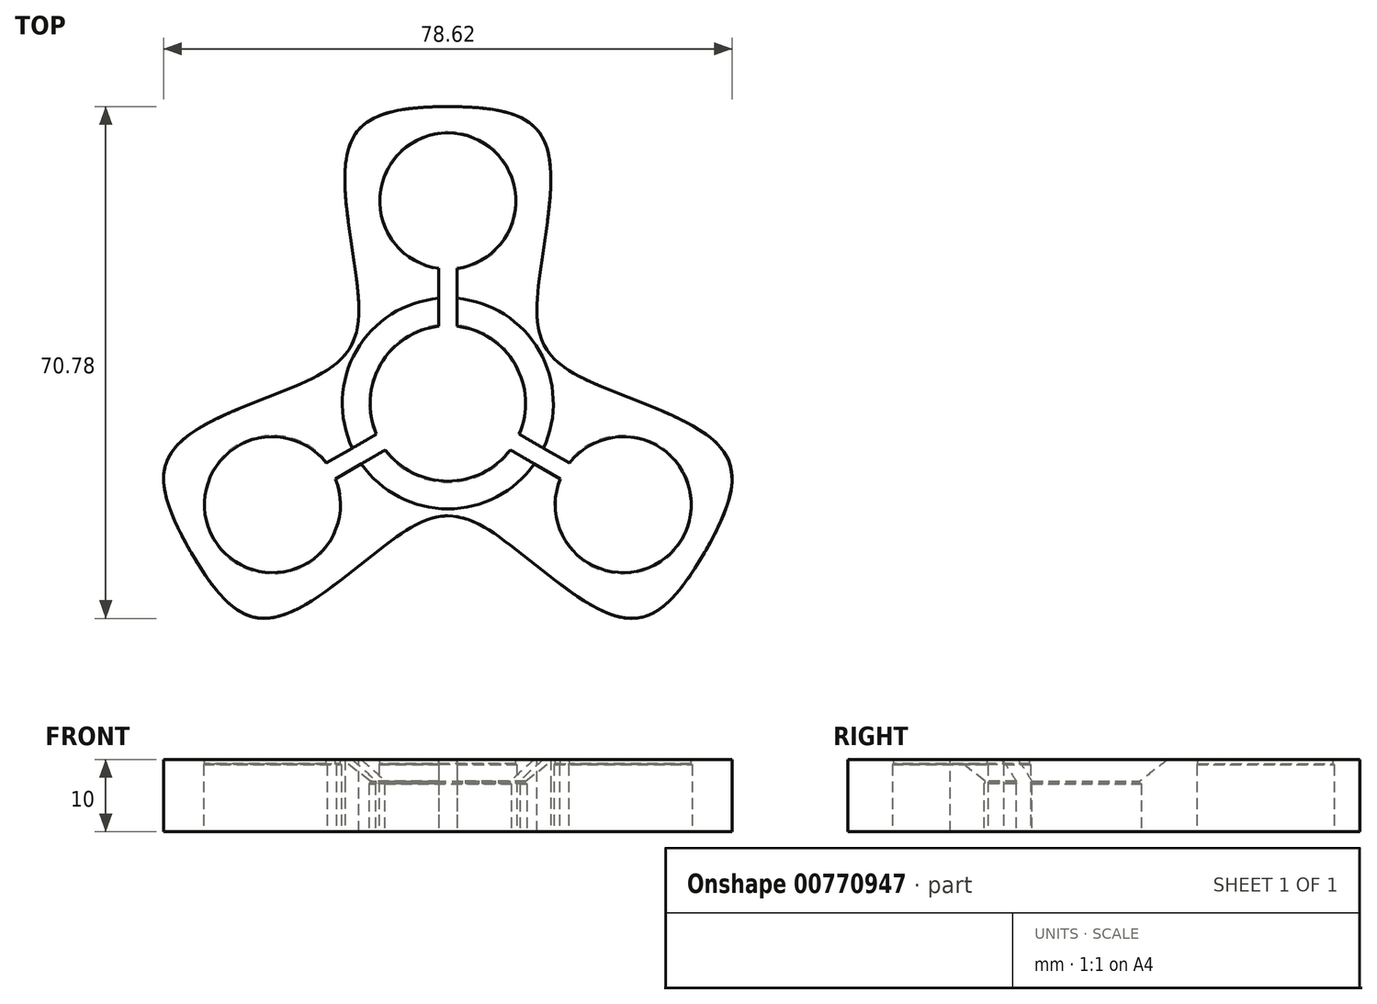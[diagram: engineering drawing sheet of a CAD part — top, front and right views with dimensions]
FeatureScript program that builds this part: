
annotation { "Feature Type Name" : "Feature", "Feature Type Description" : "" }
export const myFeature = defineFeature(function(context is Context, id is Id, definition is map)
    precondition{}
    {
        {
            assignVariable(context, id + "F0", {"name" : "ledge", "anyValue" : 0.15});
        }
        {
            var Q0;
            Q0=qCreatedBy(makeId("Top.planeOp"),FACE);
            var sketch = newSketch(context, id + "F1", { "sketchPlane" : qUnion([Q0])});
            skLineSegment(sketch, "E0", {"start": v(0, 0) * mm, "end": v(71.1, 41.05) * mm, "construction": true});
            skLineSegment(sketch, "E1", {"start": v(0, 0) * mm, "end": v(-71.1, 41.05) * mm, "construction": true});
            skCircle(sketch, "E2", {"center": v(0, 0) * mm, "radius": 10.9 * mm, "construction": true});
            skCircle(sketch, "E3", {"center": v(0, 28) * mm, "radius": 9.55 * mm});
            skLineSegment(sketch, "E4", {"start": v(-16, 41.05) * mm, "end": v(16, 41.05) * mm});
            skLineSegment(sketch, "E5", {"start": v(16, 41.05) * mm, "end": v(11.13, 6.43) * mm});
            skLineSegment(sketch, "E6", {"start": v(-16, 41.05) * mm, "end": v(-11.13, 6.43) * mm});
            skLineSegment(sketch, "E7", {"start": v(0, 28) * mm, "end": v(0, 41.05) * mm, "construction": true});
            skPoint(sketch, "E8", {"position": v(0, 37.55) * mm});
            skArc(sketch, "E9", {"start": v(9.44, 5.45) * mm, "mid": v(0, 10.9) * mm, "end": v(-9.44, 5.45) * mm});
            skLineSegment(sketch, "E10", {"start": v(-9.44, 5.45) * mm, "end": v(-11.13, 6.43) * mm});
            skLineSegment(sketch, "E11", {"start": v(9.44, 5.45) * mm, "end": v(11.13, 6.43) * mm});
            skSolve(sketch);
        }
        {
            var Q0;
            Q0=qSketchRegion(id+"F1",true);
            extrude(context, id + "F2", {"entities" : qUnion([Q0]), "endBound" : BoundingType.SYMMETRIC, "depth" : 7 * mm, "offsetDistance" : 25 * mm});
        }
        {
            var Q0;
            Q0=makeQuery(id+"F2.opExtrude","SWEPT_EDGE",EDGE,{"disambiguationData":[OSD([sQuery(id+"F1.wireOp",EDGE,"E4"),sQuery(id+"F1.wireOp",EDGE,"E6")])]});
            var Q1;
            Q1=makeQuery(id+"F2.opExtrude","SWEPT_EDGE",EDGE,{"disambiguationData":[OSD([sQuery(id+"F1.wireOp",EDGE,"E4"),sQuery(id+"F1.wireOp",EDGE,"E5")])]});
            fillet(context, id + "F3", {"entities" : qUnion([Q0, Q1]), "radius" : 14 * mm, "tangentPropagation" : true, "rho" : .6, "crossSection" : FilletCrossSection.CONIC, "allowEdgeOverflow" : false});
        }
        {
            var Q0;
            Q0=makeQuery(id+"F2.opExtrude","CAP_FACE",FACE,{"disambiguationData":[OSD([sQuery(id+"F1.wireOp",EDGE,"E3"),sQuery(id+"F1.wireOp",EDGE,"E4"),sQuery(id+"F1.wireOp",EDGE,"E5"),sQuery(id+"F1.wireOp",EDGE,"E6"),sQuery(id+"F1.wireOp",EDGE,"E9"),sQuery(id+"F1.wireOp",EDGE,"E10"),sQuery(id+"F1.wireOp",EDGE,"E11")])],"isStart":false});
            var sketch = newSketch(context, id + "F4", { "sketchPlane" : qUnion([Q0])});
            skCircle(sketch, "E12.0", {"center": v(0, 28) * mm, "radius": 9.55 * mm});
            skCircle(sketch, "E13.0", {"center": v(0, 28) * mm, "radius": 9.4 * mm});
            skArc(sketch, "E14.0", {"start": v(9.44, 5.45) * mm, "mid": v(0, 10.9) * mm, "end": v(-9.44, 5.45) * mm});
            skArc(sketch, "E15.0", {"start": v(9.3, 5.37) * mm, "mid": v(0, 10.75) * mm, "end": v(-9.3, 5.37) * mm});
            skLineSegment(sketch, "E16", {"start": v(-9.3, 5.37) * mm, "end": v(-9.44, 5.45) * mm});
            skLineSegment(sketch, "E17", {"start": v(9.3, 5.37) * mm, "end": v(9.44, 5.45) * mm});
            skSolve(sketch);
        }
        {
            var Q0;
            Q0=makeQuery(id+"F4.imprint","IMPRINT",FACE,{"disambiguationData":[TD([[makeQuery(id+"F4.imprint","IMPRINT",EDGE,{"derivedFrom":sQuery(id+"F4.wireOp",EDGE,"E14.0")}),1.0]])]});
            extrude(context, id + "F5", {"entities" : qUnion([Q0]), "operationType" : NewBodyOperationType.ADD, "oppositeDirection" : true, "depth" : .4 * mm, "offsetDistance" : 25 * mm});
        }
        {
            var Q0;
            Q0=makeQuery(id+"F5.boolean.opBoolean","MERGE",FACE,{"derivedFrom":[makeQuery(id+"F2.opExtrude","CAP_FACE",FACE,{"disambiguationData":[OSD([sQuery(id+"F1.wireOp",EDGE,"E3"),sQuery(id+"F1.wireOp",EDGE,"E4"),sQuery(id+"F1.wireOp",EDGE,"E5"),sQuery(id+"F1.wireOp",EDGE,"E6"),sQuery(id+"F1.wireOp",EDGE,"E9"),sQuery(id+"F1.wireOp",EDGE,"E10"),sQuery(id+"F1.wireOp",EDGE,"E11")])],"isStart":false}),makeQuery(id+"F5.opExtrude","CAP_FACE",FACE,{"disambiguationData":[OSD([sQuery(id+"F4.wireOp",EDGE,"E14.0"),sQuery(id+"F4.wireOp",EDGE,"E15.0"),sQuery(id+"F4.wireOp",EDGE,"E16"),sQuery(id+"F4.wireOp",EDGE,"E17")])],"isStart":true})]});
            extrude(context, id + "F6", {"entities" : qUnion([Q0]), "operationType" : NewBodyOperationType.ADD, "depth" : 3 * mm, "offsetDistance" : 25 * mm});
        }
        {
            var Q0;
            Q0=makeQuery(id+"F6.opExtrude","CAP_FACE",FACE,{"disambiguationData":[OSD([sQuery(id+"F1.wireOp",EDGE,"E3"),sQuery(id+"F1.wireOp",EDGE,"E4"),sQuery(id+"F1.wireOp",EDGE,"E5"),sQuery(id+"F1.wireOp",EDGE,"E6"),sQuery(id+"F1.wireOp",EDGE,"E9"),sQuery(id+"F1.wireOp",EDGE,"E10"),sQuery(id+"F1.wireOp",EDGE,"E11"),sQuery(id+"F4.wireOp",EDGE,"E14.0"),sQuery(id+"F4.wireOp",EDGE,"E15.0"),sQuery(id+"F4.wireOp",EDGE,"E16"),sQuery(id+"F4.wireOp",EDGE,"E17")])],"isStart":false});
            var sketch = newSketch(context, id + "F7", { "sketchPlane" : qUnion([Q0])});
            skCircle(sketch, "E18.0", {"center": v(0, 28) * mm, "radius": 9.4 * mm});
            skCircle(sketch, "E19.0", {"center": v(0, 28) * mm, "radius": 9.55 * mm});
            skSolve(sketch);
        }
        {
            var Q0;
            Q0=qSketchRegion(id+"F7",true);
            extrude(context, id + "F8", {"entities" : qUnion([Q0]), "operationType" : NewBodyOperationType.ADD, "oppositeDirection" : true, "depth" : .75 * mm, "offsetDistance" : 25 * mm});
        }
        {
            var Q0;
            Q0=makeQuery(id+"F5.opExtrude","CAP_EDGE",EDGE,{"disambiguationData":[OSD([sQuery(id+"F4.wireOp",EDGE,"E13.0")])],"isStart":false});
            var Q1;
            Q1=makeQuery(id+"F5.opExtrude","CAP_EDGE",EDGE,{"disambiguationData":[OSD([sQuery(id+"F4.wireOp",EDGE,"E15.0")])],"isStart":false});
            var Q2;
            Q2=makeQuery(id+"F8.opExtrude","CAP_EDGE",EDGE,{"disambiguationData":[OSD([sQuery(id+"F7.wireOp",EDGE,"E18.0")])],"isStart":false});
            chamfer(context, id + "F9", {"entities" : qUnion([Q0, Q1, Q2]), "width" : (getVariable(context, 'ledge')) * mm, "tangentPropagation" : true});
        }
        {
            var Q0;
            Q0=makeQuery(id+"F6.opExtrude","CAP_EDGE",EDGE,{"disambiguationData":[OSD([sQuery(id+"F4.wireOp",EDGE,"E15.0")])],"isStart":false});
            chamfer(context, id + "F10", {"entities" : qUnion([Q0]), "chamferType" : ChamferType.OFFSET_ANGLE, "width" : 3 * mm, "oppositeDirection" : false, "angle" : 52 * degree, "tangentPropagation" : true});
        }
        {
            var Q0;
            Q0=qCreatedBy(makeId("Top.planeOp"),FACE);
            var sketch = newSketch(context, id + "F11", { "sketchPlane" : qUnion([Q0])});
            skLineSegment(sketch, "E20.bottom", {"start": v(-1.25, 0) * mm, "end": v(1.25, 0) * mm});
            skLineSegment(sketch, "E20.top", {"start": v(-1.25, 28) * mm, "end": v(1.25, 28) * mm});
            skLineSegment(sketch, "E20.left", {"start": v(-1.25, 0) * mm, "end": v(-1.25, 28) * mm});
            skLineSegment(sketch, "E20.right", {"start": v(1.25, 0) * mm, "end": v(1.25, 28) * mm});
            skPoint(sketch, "E21", {"position": v(0, 28) * mm});
            skSolve(sketch);
        }
        {
            var Q0;
            Q0=makeQuery(id+"F11.imprint","IMPRINT",FACE,{"disambiguationData":[TD([[makeQuery(id+"F11.imprint","IMPRINT",EDGE,{"derivedFrom":sQuery(id+"F11.wireOp",EDGE,"E20.bottom")}),1.0]])]});
            extrude(context, id + "F12", {"entities" : qUnion([Q0]), "operationType" : NewBodyOperationType.REMOVE, "endBound" : BoundingType.THROUGH_ALL, "depth" : 25 * mm, "offsetDistance" : 25 * mm, "hasSecondDirection" : true, "secondDirectionBound" : SecondDirectionBoundingType.THROUGH_ALL, "secondDirectionOppositeDirection" : true, "secondDirectionDepth" : 25 * mm});
        }
        {
            var Q0;
            Q0=qCreatedBy(makeId("Front.planeOp"),FACE);
            var sketch = newSketch(context, id + "F13", { "sketchPlane" : qUnion([Q0])});
            skLineSegment(sketch, "E22", {"start": v(0, 0) * mm, "end": v(0, 20.55) * mm, "construction": true});
            skSolve(sketch);
        }
        {
            var Q0;
            Q0=makeQuery(id+"F2.opExtrude","SWEPT_BODY",BODY,{"disambiguationData":[OSD([sQuery(id+"F1.wireOp",EDGE,"E3"),sQuery(id+"F1.wireOp",EDGE,"E4"),sQuery(id+"F1.wireOp",EDGE,"E5"),sQuery(id+"F1.wireOp",EDGE,"E6"),sQuery(id+"F1.wireOp",EDGE,"E9"),sQuery(id+"F1.wireOp",EDGE,"E10"),sQuery(id+"F1.wireOp",EDGE,"E11")])]});
            var Q1;
            Q1=sQuery(id+"F13.wireOp",EDGE,"E22");
            circularPattern(context, id + "F14", {"operationType" : NewBodyOperationType.ADD, "entities" : qUnion([Q0]), "axis" : qUnion([Q1]), "angle" : 360 * degree, "instanceCount" : 3, "equalSpace" : true});
        }
        {
            var Q0;
            Q0=makeQuery(id+"F14.boolean.opBoolean","MERGE",EDGE,{"derivedFrom":[makeQuery(id+"F2.opExtrude","SWEPT_EDGE",EDGE,{"disambiguationData":[OSD([sQuery(id+"F1.wireOp",EDGE,"E5"),sQuery(id+"F1.wireOp",EDGE,"E11")])]}),makeQuery(id+"F14.opPattern","COPY",EDGE,{"derivedFrom":makeQuery(id+"F2.opExtrude","SWEPT_EDGE",EDGE,{"disambiguationData":[OSD([sQuery(id+"F1.wireOp",EDGE,"E6"),sQuery(id+"F1.wireOp",EDGE,"E10")])]}),"instanceName":"2"})]});
            var Q1;
            Q1=makeQuery(id+"F14.boolean.opBoolean","MERGE",EDGE,{"derivedFrom":[makeQuery(id+"F2.opExtrude","SWEPT_EDGE",EDGE,{"disambiguationData":[OSD([sQuery(id+"F1.wireOp",EDGE,"E6"),sQuery(id+"F1.wireOp",EDGE,"E10")])]}),makeQuery(id+"F14.opPattern","COPY",EDGE,{"derivedFrom":makeQuery(id+"F2.opExtrude","SWEPT_EDGE",EDGE,{"disambiguationData":[OSD([sQuery(id+"F1.wireOp",EDGE,"E5"),sQuery(id+"F1.wireOp",EDGE,"E11")])]}),"instanceName":"1"})]});
            var Q2;
            Q2=makeQuery(id+"F14.boolean.opBoolean","MERGE",EDGE,{"derivedFrom":[makeQuery(id+"F14.opPattern","COPY",EDGE,{"derivedFrom":makeQuery(id+"F2.opExtrude","SWEPT_EDGE",EDGE,{"disambiguationData":[OSD([sQuery(id+"F1.wireOp",EDGE,"E6"),sQuery(id+"F1.wireOp",EDGE,"E10")])]}),"instanceName":"1"}),makeQuery(id+"F14.opPattern","COPY",EDGE,{"derivedFrom":makeQuery(id+"F2.opExtrude","SWEPT_EDGE",EDGE,{"disambiguationData":[OSD([sQuery(id+"F1.wireOp",EDGE,"E5"),sQuery(id+"F1.wireOp",EDGE,"E11")])]}),"instanceName":"2"})]});
            fillet(context, id + "F15", {"entities" : qUnion([Q0, Q1, Q2]), "radius" : 14 * mm, "tangentPropagation" : true, "rho" : .6, "crossSection" : FilletCrossSection.CONIC, "allowEdgeOverflow" : false});
        }
    });
